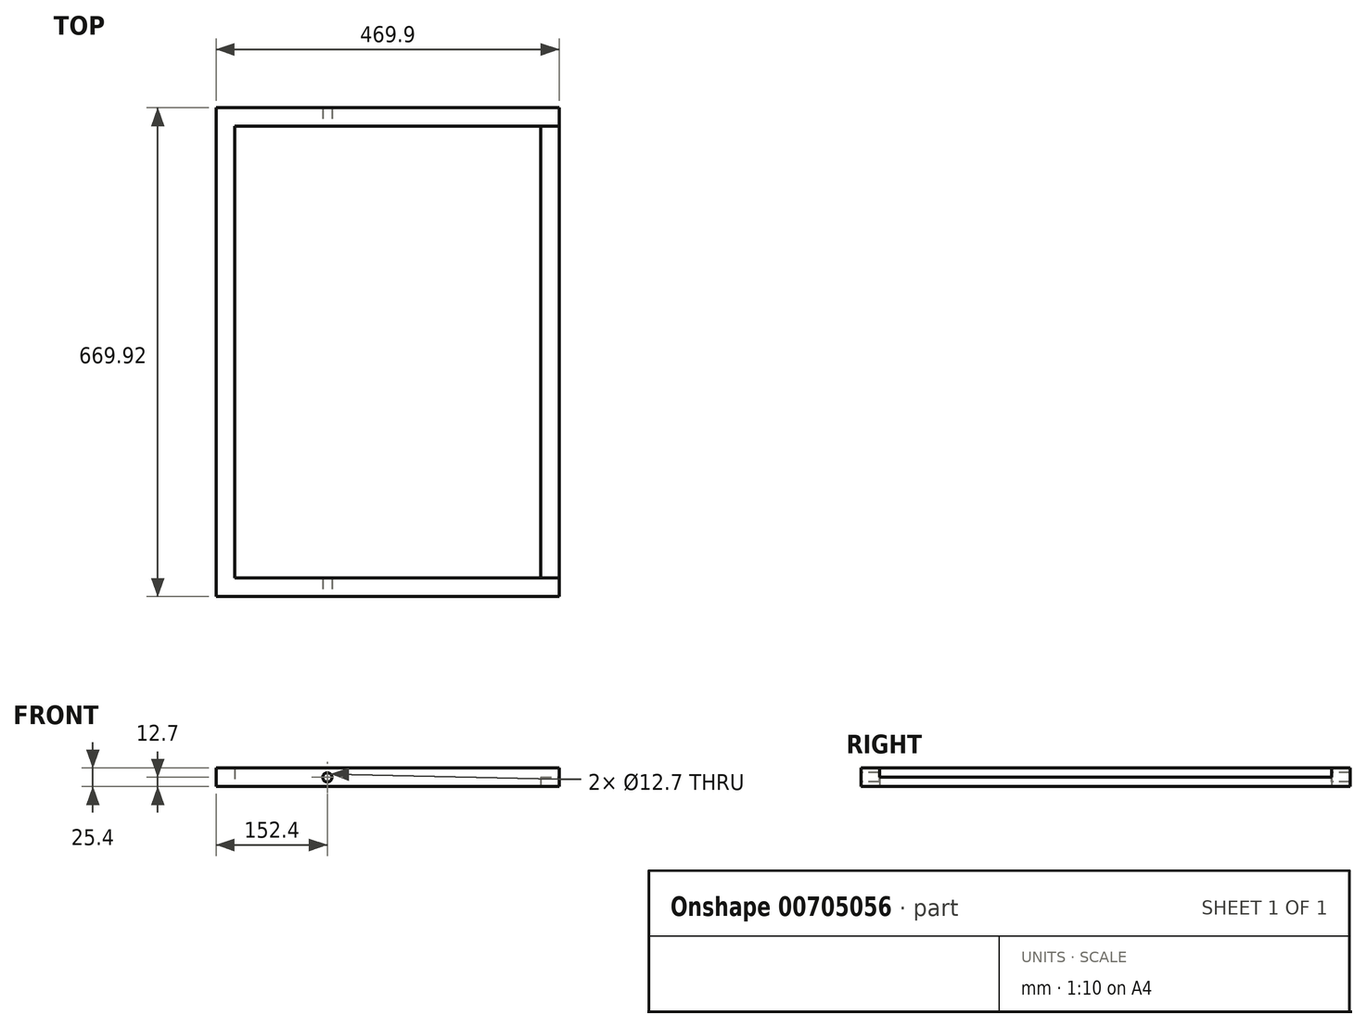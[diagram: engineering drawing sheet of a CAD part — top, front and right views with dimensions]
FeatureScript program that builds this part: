
annotation { "Feature Type Name" : "Feature", "Feature Type Description" : "" }
export const myFeature = defineFeature(function(context is Context, id is Id, definition is map)
    precondition{}
    {
        {
            var Q0;
            Q0=qCreatedBy(makeId("Top.planeOp"),FACE);
            var sketch = newSketch(context, id + "F0", { "sketchPlane" : qUnion([Q0])});
            skLineSegment(sketch, "E0.bottom", {"start": v(-234.95, 334.96) * mm, "end": v(234.95, 334.96) * mm});
            skLineSegment(sketch, "E0.top", {"start": v(-234.95, -334.96) * mm, "end": v(234.95, -334.96) * mm});
            skLineSegment(sketch, "E0.left", {"start": v(-234.95, 334.96) * mm, "end": v(-234.95, -334.96) * mm});
            skLineSegment(sketch, "E0.right", {"start": v(234.95, 334.96) * mm, "end": v(234.95, -334.96) * mm});
            skPoint(sketch, "E1", {"position": v(0, 334.96) * mm});
            skPoint(sketch, "E2", {"position": v(-234.95, 0) * mm});
            skLineSegment(sketch, "E3.bottom", {"start": v(-209.55, 309.56) * mm, "end": v(209.55, 309.56) * mm});
            skLineSegment(sketch, "E3.top", {"start": v(-209.55, -309.56) * mm, "end": v(209.55, -309.56) * mm});
            skLineSegment(sketch, "E3.left", {"start": v(-209.55, 309.56) * mm, "end": v(-209.55, -309.56) * mm});
            skLineSegment(sketch, "E3.right", {"start": v(209.55, 309.56) * mm, "end": v(209.55, -309.56) * mm});
            skLineSegment(sketch, "E4", {"start": v(209.55, 309.56) * mm, "end": v(234.95, 309.56) * mm});
            skLineSegment(sketch, "E5", {"start": v(209.55, -309.56) * mm, "end": v(234.95, -309.56) * mm});
            skSolve(sketch);
        }
        {
            var Q0;
            {var subQ1=sQuery(id+"F0.wireOp",EDGE,"E0.bottom");Q0=makeQuery(id+"F0.imprint","IMPRINT",FACE,{"disambiguationData":[TD([[makeQuery(id+"F0.imprint","IMPRINT",EDGE,{"derivedFrom":subQ1}),-1.0]])]});}
            extrude(context, id + "F1", {"entities" : qUnion([Q0]), "depth" : 25.4 * mm, "offsetDistance" : 25.4 * mm});
        }
        {
            var Q0;
            Q0=makeQuery(id+"F0.imprint","IMPRINT",FACE,{"disambiguationData":[TD([[makeQuery(id+"F0.imprint","IMPRINT",EDGE,{"derivedFrom":sQuery(id+"F0.wireOp",EDGE,"E3.right")}),1.0]])]});
            extrude(context, id + "F2", {"entities" : qUnion([Q0]), "operationType" : NewBodyOperationType.ADD, "depth" : 12.7 * mm, "offsetDistance" : 25.4 * mm});
        }
        {
            var Q0;
            Q0=makeQuery(id+"F1.opExtrude","SWEPT_FACE",FACE,{"disambiguationData":[OSD([sQuery(id+"F0.wireOp",EDGE,"E0.top")])]});
            var sketch = newSketch(context, id + "F3", { "sketchPlane" : qUnion([Q0])});
            skPoint(sketch, "E6", {"position": v(-234.95, 12.7) * mm});
            skPoint(sketch, "E7", {"position": v(-82.55, 12.7) * mm});
            skCircle(sketch, "E8", {"center": v(-82.55, 12.7) * mm, "radius": 6.35 * mm});
            skSolve(sketch);
        }
        {
            var Q0;
            Q0=qSketchRegion(id+"F3",true);
            extrude(context, id + "F4", {"entities" : qUnion([Q0]), "operationType" : NewBodyOperationType.REMOVE, "oppositeDirection" : true, "depth" : 762 * mm, "offsetDistance" : 25.4 * mm});
        }
    });
